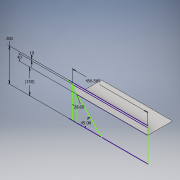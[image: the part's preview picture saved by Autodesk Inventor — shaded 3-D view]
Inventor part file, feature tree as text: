
AUTODESK INVENTOR PART (.ipt)
format: ipt  version: 2019 (Build 230136000, 136)  size: 148,992 bytes
history: native  units: mm
features: sheet_metal_op x3, sketch x2, other x1
ambient origin geometry x8: Origin, YZ Plane, XZ Plane, XY Plane, X Axis, Y Axis, Z Axis, Center Point
bodies: Solid1 (feature_tree)
feature tree (6):
  sketch  "Sketch1"  dims[d0=200.0mm]
  sheet_metal_op  "Face1"
  sheet_metal_op  "Fold2"
  sheet_metal_op  "Hem1"
  other  "Plate1"
  sketch  "Sketch2"  dims[d2=10.0mm d3=40.0mm d4=150.0mm d5=45.0deg d7=45.0deg d8=10.0mm d9=40.0mm d10=456.585472mm d12=4.886922mm d13=0.5mm d20=0.5mm d21=0.25mm d22=1.0mm d23=0.5mm d24=90.0deg d25=0.5mm d26=0.5mm d27=0.25mm d28=1.0mm d29=0.5mm d30=10.0mm d31=0.25mm d32=0.125mm]
